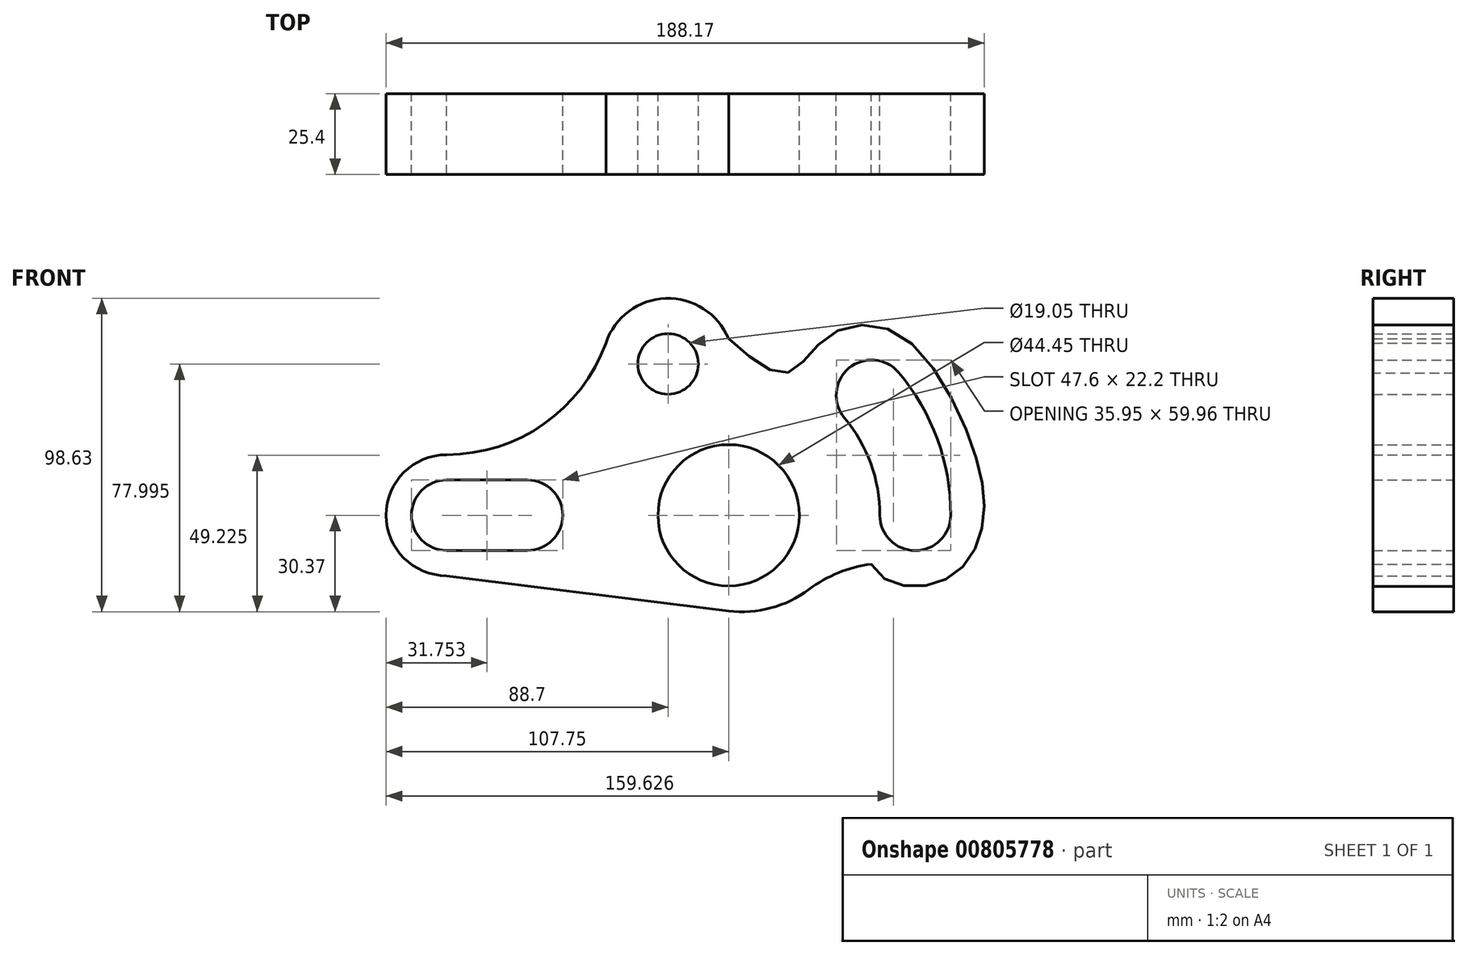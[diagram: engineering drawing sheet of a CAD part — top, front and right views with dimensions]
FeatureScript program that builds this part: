
annotation { "Feature Type Name" : "Feature", "Feature Type Description" : "" }
export const myFeature = defineFeature(function(context is Context, id is Id, definition is map)
    precondition{}
    {
        {
            var Q0;
            Q0=qCreatedBy(makeId("Front.planeOp"),FACE);
            var sketch = newSketch(context, id + "F0", { "sketchPlane" : qUnion([Q0])});
            skCircle(sketch, "E0", {"center": v(0, 0) * mm, "radius": 14.29 * mm});
            skCircle(sketch, "E1", {"center": v(0, 0) * mm, "radius": 22.23 * mm});
            skLineSegment(sketch, "E2", {"start": v(0, 0) * mm, "end": v(0, 47.63) * mm, "construction": true});
            skLineSegment(sketch, "E3", {"start": v(0, 47.63) * mm, "end": v(-19.05, 47.63) * mm, "construction": true});
            skCircle(sketch, "E4", {"center": v(-19.05, 47.63) * mm, "radius": 9.53 * mm});
            skCircle(sketch, "E5", {"center": v(-19.05, 47.63) * mm, "radius": 20.64 * mm});
            skLineSegment(sketch, "E6", {"start": v(0, 0) * mm, "end": v(-88.7, 0) * mm, "construction": true});
            skLineSegment(sketch, "E7", {"start": v(-88.7, 0) * mm, "end": v(-63.3, 0) * mm, "construction": true});
            skArc(sketch, "E8", {"start": v(-63.3, 11.1) * mm, "mid": v(-52.2, 0) * mm, "end": v(-63.3, -11.1) * mm});
            skArc(sketch, "E9.MirrorCS", {"start": v(-63.3, -11.1) * mm, "mid": v(-52.2, 0) * mm, "end": v(-63.3, 11.1) * mm});
            skArc(sketch, "E10", {"start": v(-88.7, 11.1) * mm, "mid": v(-99.8, 0) * mm, "end": v(-88.7, -11.1) * mm});
            skLineSegment(sketch, "E11", {"start": v(-63.3, 11.1) * mm, "end": v(-88.7, 11.1) * mm});
            skLineSegment(sketch, "E12", {"start": v(-88.7, -11.1) * mm, "end": v(-63.3, -11.1) * mm});
            skArc(sketch, "E13", {"start": v(-63.3, 19.05) * mm, "mid": v(-44.25, 0) * mm, "end": v(-63.3, -19.05) * mm});
            skArc(sketch, "E14", {"start": v(-88.7, 19.05) * mm, "mid": v(-107.75, 0) * mm, "end": v(-88.7, -19.05) * mm});
            skLineSegment(sketch, "E15", {"start": v(-88.7, 19.05) * mm, "end": v(-63.3, 19.05) * mm});
            skLineSegment(sketch, "E16", {"start": v(-88.7, -19.05) * mm, "end": v(-63.3, -19.05) * mm});
            skArc(sketch, "E17", {"start": v(-88.7, 19.05) * mm, "mid": v(-58.09, 28.72) * mm, "end": v(-38.6, 54.23) * mm});
            skLineSegment(sketch, "E18", {"start": v(0, 0) * mm, "end": v(58.72, 0) * mm, "construction": true});
            skArc(sketch, "E19", {"start": v(47.6, 0) * mm, "mid": v(58.72, -11.13) * mm, "end": v(69.85, 0) * mm});
            skLineSegment(sketch, "E20", {"start": v(0, 0) * mm, "end": v(44.99, 37.75) * mm, "construction": true});
            skArc(sketch, "E21", {"start": v(36.46, 30.6) * mm, "mid": v(37.8, 46.25) * mm, "end": v(53.46, 44.96) * mm});
            skArc(sketch, "E22", {"start": v(53.46, 44.96) * mm, "mid": v(65.7, 23.95) * mm, "end": v(69.85, 0) * mm});
            skArc(sketch, "E23", {"start": v(36.46, 30.6) * mm, "mid": v(44.73, 16.28) * mm, "end": v(47.6, 0) * mm});
            skLineSegment(sketch, "E24", {"start": v(-88.7, -19.05) * mm, "end": v(0, -30.1) * mm});
            skArc(sketch, "E25", {"start": v(0, -30.1) * mm, "mid": v(13.3, -29.2) * mm, "end": v(25.3, -23.36) * mm});
            skFitSpline(sketch, "E26", {"points": [v(0, 55.56) * mm, v(17.97, 44.74) * mm, v(30.5, 55.73) * mm, v(53.1, 57.26) * mm, v(76, 23.67) * mm, v(80.27, 0) * mm, v(73.55, -16.34) * mm, v(57.98, -22.45) * mm, v(44.84, -15.42) * mm], "startDerivative": vector(141.89, -127.5) * mm, "endDerivative": vector(-64.4, 134.7) * mm});
            skArc(sketch, "E27", {"start": v(25.3, -23.36) * mm, "mid": v(34.56, -18.12) * mm, "end": v(44.84, -15.42) * mm});
            skSolve(sketch);
        }
        {
            var Q0;
            Q0 = qSketchRegion(id + "F0", true);
            extrude(context, id + "F1", {"entities" : qUnion([Q0]), "depth" : 25.4 * mm, "offsetDistance" : 25.4 * mm});
        }
    });
